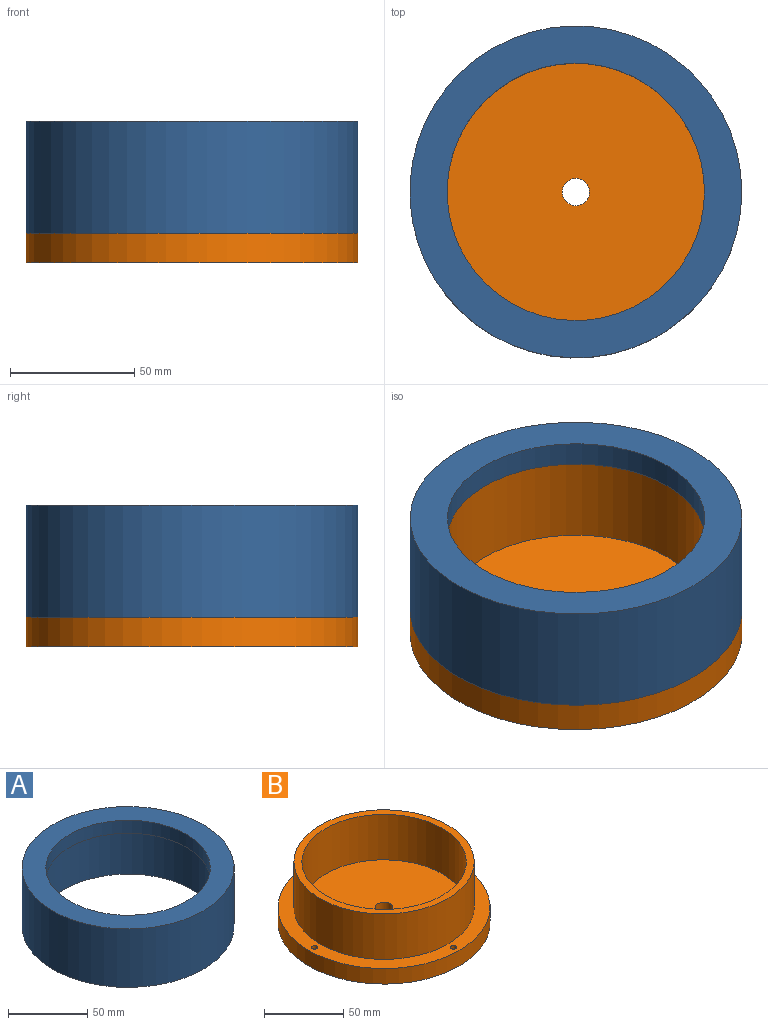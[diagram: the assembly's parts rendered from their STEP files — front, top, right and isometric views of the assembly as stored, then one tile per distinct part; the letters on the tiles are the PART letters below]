
ASSEMBLY  parts=2 mates=1
PART A: 14 faces, bbox 133.5x133.5x45 mm
  f0: cylinder r=56.75mm len=113.5mm, axis (0,0,-1), area 12480mm2, adj f3,f4
  f1: cylinder r=66.75mm len=133.5mm, axis (0,0,-1), area 18873.1mm2, adj f2,f3
  f2: plane 133.5x133.5mm, normal (0,0,1), area 5584.2mm2, adj f1,f5
  f3: plane 133.5x133.5mm, normal (0,0,-1), area 3834.6mm2, adj f0,f1,f6,f8,f10,f12
  f4: plane 113.5x113.5mm, normal (0,0,-1), area 1704.3mm2, adj f0,f5
  f5: cylinder r=51.75mm len=103.5mm, axis (0,0,1), area 3251.5mm2, adj f2,f4
  f6: cylinder r=1.9mm len=30mm, axis (0,0,-1), area 357.9mm2, adj f3,f7
  f7: plane 3.8x3.8mm, normal (0,0,-1), area 11.3mm2, adj f6
  f8: cylinder r=1.9mm len=30mm, axis (0,0,-1), area 357.9mm2, adj f3,f9
  f9: plane 3.8x3.8mm, normal (0,0,-1), area 11.3mm2, adj f8
  f10: cylinder r=1.9mm len=30mm, axis (0,0,-1), area 357.9mm2, adj f3,f11
  f11: plane 3.8x3.8mm, normal (0,0,-1), area 11.3mm2, adj f10
  f12: cylinder r=1.9mm len=30mm, axis (0,0,-1), area 357.9mm2, adj f3,f13
  f13: plane 3.8x3.8mm, normal (0,0,-1), area 11.3mm2, adj f12
PART B: 12 faces, bbox 133.5x133.5x47 mm
  f0: cylinder r=66.75mm len=133.5mm, axis (0,0,-1), area 5032.8mm2, adj f1,f2
  f1: plane 133.5x133.5mm, normal (0,0,1), area 3834.6mm2, adj f0,f4,f7,f8,f9,f10
  f2: plane 133.5x133.5mm, normal (0,0,-1), area 13857.2mm2, adj f0,f7,f8,f9,f10,f11
  f3: cylinder r=51.75mm len=103.5mm, axis (0,0,-1), area 11380.4mm2, adj f5,f6
  f4: cylinder r=56.75mm len=113.5mm, axis (0,0,-1), area 12480mm2, adj f1,f5
  f5: plane 113.5x113.5mm, normal (0,0,1), area 1704.3mm2, adj f3,f4
  f6: plane 103.5x103.5mm, normal (0,0,1), area 8318.3mm2, adj f3,f11
  f7: cylinder r=1.9mm len=12mm, axis (0,0,-1), area 143.1mm2, adj f1,f2
  f8: cylinder r=1.9mm len=12mm, axis (0,0,-1), area 143.1mm2, adj f1,f2
  f9: cylinder r=1.9mm len=12mm, axis (0,0,-1), area 143.1mm2, adj f1,f2
  f10: cylinder r=1.9mm len=12mm, axis (0,0,-1), area 143.1mm2, adj f1,f2
  f11: cylinder r=5.5mm len=12mm, axis (0,0,-1), area 414.7mm2, adj f2,f6
PLACE A t=(24.16,-35.54,-85.73)mm
PLACE B t=(24.16,-35.54,-97.73)mm
MATE slider A.f0 <-> B.f0  axis (0,0,-1) through (24.16,-35.54,-85.73)mm
